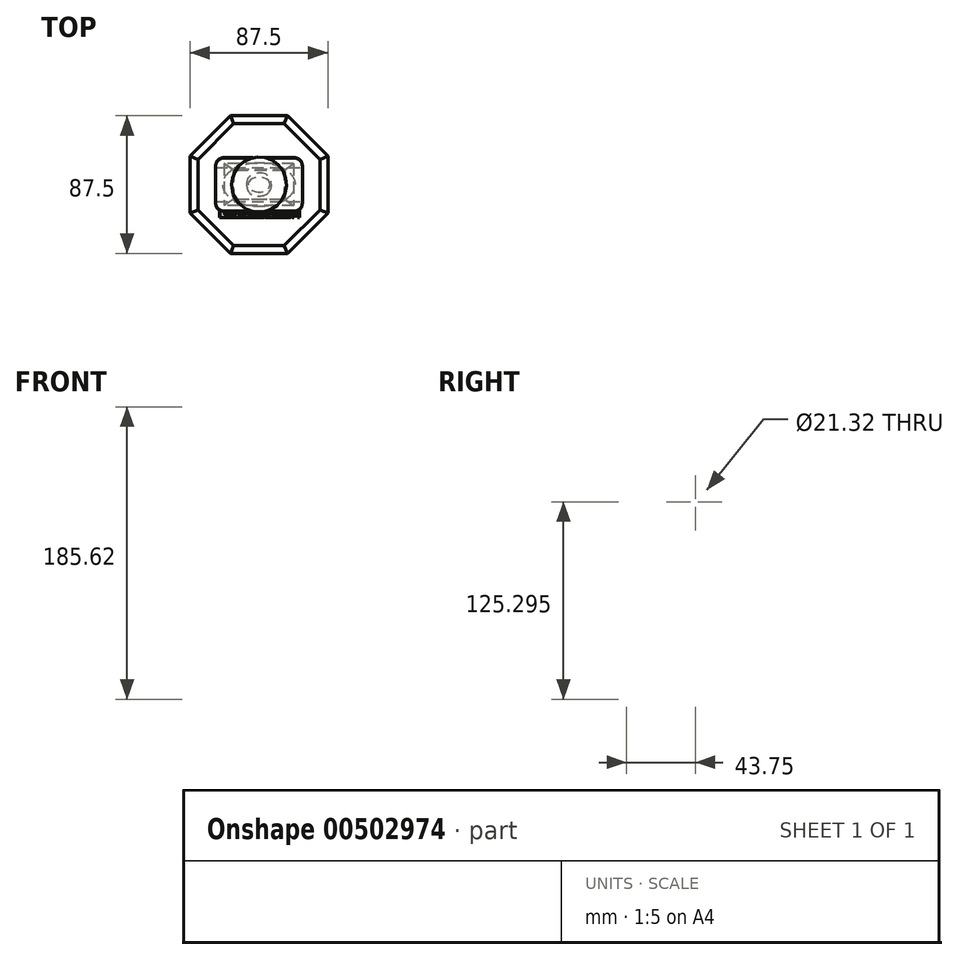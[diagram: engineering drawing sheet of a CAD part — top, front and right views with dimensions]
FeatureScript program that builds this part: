
annotation { "Feature Type Name" : "Feature", "Feature Type Description" : "" }
export const myFeature = defineFeature(function(context is Context, id is Id, definition is map)
    precondition{}
    {
        {
            var Q0;
            Q0=qCreatedBy(makeId("Top.planeOp"),FACE);
            cPlane(context, id + "F0", {"entities" : qUnion([Q0]), "cplaneType" : CPlaneType.OFFSET, "offset" : 60 * mm, "oppositeDirection" : true, "width" : 150 * mm, "height" : 150 * mm});
        }
        {
            var Q0;
            Q0=qCreatedBy(id+"F0.planeOp",FACE);
            var sketch = newSketch(context, id + "F1", { "sketchPlane" : qUnion([Q0])});
            skLineSegment(sketch, "E0.bottom", {"start": v(22.05, 13.3) * mm, "end": v(-22.05, 13.3) * mm});
            skLineSegment(sketch, "E0.top", {"start": v(22.05, -13.3) * mm, "end": v(-22.05, -13.3) * mm});
            skLineSegment(sketch, "E0.left", {"start": v(22.05, 13.3) * mm, "end": v(22.05, -13.3) * mm});
            skLineSegment(sketch, "E0.right", {"start": v(-22.05, 13.3) * mm, "end": v(-22.05, -13.3) * mm});
            skPoint(sketch, "E0.middle", {"position": v(0, 0) * mm});
            skSolve(sketch);
        }
        {
            var Q0;
            Q0=qCreatedBy(id+"F0.planeOp",FACE);
            cPlane(context, id + "F2", {"entities" : qUnion([Q0]), "cplaneType" : CPlaneType.OFFSET, "offset" : 30 * mm, "oppositeDirection" : true, "width" : 150 * mm, "height" : 150 * mm});
        }
        {
            var Q0;
            Q0=qCreatedBy(id+"F2.planeOp",FACE);
            var sketch = newSketch(context, id + "F3", { "sketchPlane" : qUnion([Q0])});
            skLineSegment(sketch, "E1.bottom", {"start": v(13.98, 7.39) * mm, "end": v(-13.98, 7.39) * mm});
            skLineSegment(sketch, "E1.top", {"start": v(13.98, -7.39) * mm, "end": v(-13.98, -7.39) * mm});
            skLineSegment(sketch, "E1.left", {"start": v(13.98, 7.39) * mm, "end": v(13.98, -7.39) * mm});
            skLineSegment(sketch, "E1.right", {"start": v(-13.98, 7.39) * mm, "end": v(-13.98, -7.39) * mm});
            skPoint(sketch, "E1.middle", {"position": v(0, 0) * mm});
            skSolve(sketch);
        }
        {
            var Q0;
            Q0=qCreatedBy(id+"F0.planeOp",FACE);
            cPlane(context, id + "F4", {"entities" : qUnion([Q0]), "cplaneType" : CPlaneType.OFFSET, "offset" : 10 * mm, "oppositeDirection" : true, "width" : 150 * mm, "height" : 150 * mm});
        }
        {
            var Q0;
            Q0=qCreatedBy(id+"F4.planeOp",FACE);
            var sketch = newSketch(context, id + "F5", { "sketchPlane" : qUnion([Q0])});
            skLineSegment(sketch, "E2.bottom", {"start": v(17.61, 10.11) * mm, "end": v(-17.61, 10.11) * mm});
            skLineSegment(sketch, "E2.top", {"start": v(17.61, -10.11) * mm, "end": v(-17.61, -10.11) * mm});
            skLineSegment(sketch, "E2.left", {"start": v(17.61, 10.11) * mm, "end": v(17.61, -10.11) * mm});
            skLineSegment(sketch, "E2.right", {"start": v(-17.61, 10.11) * mm, "end": v(-17.61, -10.11) * mm});
            skPoint(sketch, "E2.middle", {"position": v(0, 0) * mm});
            skSolve(sketch);
        }
        {
            var Q0;
            Q0=makeQuery(id+"F3.imprint","IMPRINT",FACE,{"disambiguationData":[TD([[makeQuery(id+"F3.imprint","IMPRINT",EDGE,{"derivedFrom":sQuery(id+"F3.wireOp",EDGE,"E1.bottom")}),1.0]])]});
            var Q1;
            Q1=makeQuery(id+"F5.imprint","IMPRINT",FACE,{"disambiguationData":[TD([[makeQuery(id+"F5.imprint","IMPRINT",EDGE,{"derivedFrom":sQuery(id+"F5.wireOp",EDGE,"E2.bottom")}),1.0]])]});
            var Q2;
            Q2=makeQuery(id+"F1.imprint","IMPRINT",FACE,{"disambiguationData":[TD([[makeQuery(id+"F1.imprint","IMPRINT",EDGE,{"derivedFrom":sQuery(id+"F1.wireOp",EDGE,"E0.bottom")}),1.0]])]});
            loft(context, id + "F6", {"sheetProfilesArray" : [{ "sheetProfileEntities" : qUnion([Q0]) }, { "sheetProfileEntities" : qUnion([Q1]) }, { "sheetProfileEntities" : qUnion([Q2]) }]});
        }
        {
            var Q0;
            Q0=qCreatedBy(id+"F0.planeOp",FACE);
            cPlane(context, id + "F7", {"entities" : qUnion([Q0]), "cplaneType" : CPlaneType.OFFSET, "offset" : 5 * mm, "width" : 150 * mm, "height" : 150 * mm});
        }
        {
            var Q0;
            Q0=qCreatedBy(id+"F7.planeOp",FACE);
            var sketch = newSketch(context, id + "F8", { "sketchPlane" : qUnion([Q0])});
            skLineSegment(sketch, "E3.bottom", {"start": v(16.62, 9.58) * mm, "end": v(-16.62, 9.58) * mm});
            skLineSegment(sketch, "E3.top", {"start": v(16.62, -9.58) * mm, "end": v(-16.62, -9.58) * mm});
            skLineSegment(sketch, "E3.left", {"start": v(16.62, 9.58) * mm, "end": v(16.62, -9.58) * mm});
            skLineSegment(sketch, "E3.right", {"start": v(-16.62, 9.58) * mm, "end": v(-16.62, -9.58) * mm});
            skPoint(sketch, "E3.middle", {"position": v(0, 0) * mm});
            skSolve(sketch);
        }
        {
            var Q1;
            Q1=makeQuery(id+"F8.imprint","IMPRINT",FACE,{"disambiguationData":[TD([[makeQuery(id+"F8.imprint","IMPRINT",EDGE,{"derivedFrom":sQuery(id+"F8.wireOp",EDGE,"E3.bottom")}),1.0]])]});
            var Q2;
            Q2=makeQuery(id+"F6.opLoft","CAP_FACE",FACE,{"disambiguationData":[OSD([makeQuery(id+"F1.imprint","IMPRINT",FACE,{"disambiguationData":[TD([[makeQuery(id+"F1.imprint","IMPRINT",EDGE,{"derivedFrom":sQuery(id+"F1.wireOp",EDGE,"E0.bottom")}),1.0]])]})])],"isStart":true});
            loft(context, id + "F9", {"operationType" : NewBodyOperationType.ADD, "sheetProfilesArray" : [{ "sheetProfileEntities" : qUnion([Q1]) }, { "sheetProfileEntities" : qUnion([Q2]) }]});
        }
        {
            var Q0;
            Q0=makeQuery(id+"F9.opLoft","CAP_FACE",FACE,{"disambiguationData":[OSD([makeQuery(id+"F8.imprint","IMPRINT",FACE,{"disambiguationData":[TD([[makeQuery(id+"F8.imprint","IMPRINT",EDGE,{"derivedFrom":sQuery(id+"F8.wireOp",EDGE,"E3.bottom")}),1.0]])]})])],"isStart":true});
            var sketch = newSketch(context, id + "F10", { "sketchPlane" : qUnion([Q0])});
            skSolve(sketch);
        }
        {
            var Q0;
            {var subQ0=sQuery(id+"F8.wireOp",EDGE,"E3.right");var subQ1=sQuery(id+"F8.wireOp",EDGE,"E3.left");var subQ2=sQuery(id+"F8.wireOp",EDGE,"E3.bottom");Q0=makeQuery(id+"F10.imprint","IMPRINT",FACE,{"disambiguationData":[TD([[makeQuery(id+"F10.imprint","IMPRINT",EDGE,{"derivedFrom":makeQuery(id+"F9.opLoft","MID_CAP_EDGE",EDGE,{"disambiguationData":[OSD([subQ2,subQ1,subQ0])],"capPos":0.0})}),-1.0]])]});}
            var sketch = newSketch(context, id + "F11", { "sketchPlane" : qUnion([Q0])});
            skEllipse(sketch, "E4", {"center": v(0, 0) * mm, "majorRadius": 6.96 * mm, "minorRadius": 4.81 * mm, "majorAxis": v(1, 0)});
            skSolve(sketch);
        }
        {
            var Q0;
            Q0=qCreatedBy(makeId("Top.planeOp"),FACE);
            var sketch = newSketch(context, id + "F12", { "sketchPlane" : qUnion([Q0])});
            skEllipse(sketch, "E5", {"center": v(0, 0) * mm, "majorRadius": 23.18 * mm, "minorRadius": 13.67 * mm, "majorAxis": v(1, 0)});
            skSolve(sketch);
        }
        {
            var Q0;
            Q0=qCreatedBy(makeId("Top.planeOp"),FACE);
            cPlane(context, id + "F13", {"entities" : qUnion([Q0]), "cplaneType" : CPlaneType.OFFSET, "offset" : 15 * mm, "oppositeDirection" : true, "width" : 150 * mm, "height" : 150 * mm});
        }
        {
            var Q0;
            Q0=qCreatedBy(id+"F13.planeOp",FACE);
            var sketch = newSketch(context, id + "F14", { "sketchPlane" : qUnion([Q0])});
            skEllipse(sketch, "E6", {"center": v(0, 0) * mm, "majorRadius": 15.9 * mm, "minorRadius": 9.58 * mm, "majorAxis": v(1, 0)});
            skSolve(sketch);
        }
        {
            var Q1;
            Q1=makeQuery(id+"F11.imprint","IMPRINT",FACE,{"disambiguationData":[TD([[makeQuery(id+"F11.imprint","IMPRINT",EDGE,{"derivedFrom":sQuery(id+"F11.wireOp",EDGE,"E4")}),1.0]])]});
            var Q2;
            Q2=makeQuery(id+"F14.imprint","IMPRINT",FACE,{"disambiguationData":[TD([[makeQuery(id+"F14.imprint","IMPRINT",EDGE,{"derivedFrom":sQuery(id+"F14.wireOp",EDGE,"E6")}),1.0]])]});
            var Q3;
            Q3=makeQuery(id+"F12.imprint","IMPRINT",FACE,{"disambiguationData":[TD([[makeQuery(id+"F12.imprint","IMPRINT",EDGE,{"derivedFrom":sQuery(id+"F12.wireOp",EDGE,"E5")}),1.0]])]});
            loft(context, id + "F15", {"operationType" : NewBodyOperationType.ADD, "sheetProfilesArray" : [{ "sheetProfileEntities" : qUnion([Q1]) }, { "sheetProfileEntities" : qUnion([Q2]) }, { "sheetProfileEntities" : qUnion([Q3]) }]});
        }
        {
            var Q0;
            Q0=qCreatedBy(makeId("Top.planeOp"),FACE);
            cPlane(context, id + "F16", {"entities" : qUnion([Q0]), "cplaneType" : CPlaneType.OFFSET, "offset" : 5 * mm, "width" : 150 * mm, "height" : 150 * mm});
        }
        {
            var Q0;
            Q0=qCreatedBy(makeId("Top.planeOp"),FACE);
            cPlane(context, id + "F17", {"entities" : qUnion([Q0]), "cplaneType" : CPlaneType.OFFSET, "offset" : 50 * mm, "width" : 150 * mm, "height" : 150 * mm});
        }
        {
            var Q0;
            Q0=qCreatedBy(id+"F17.planeOp",FACE);
            cPlane(context, id + "F18", {"entities" : qUnion([Q0]), "cplaneType" : CPlaneType.OFFSET, "offset" : 10 * mm, "width" : 150 * mm, "height" : 150 * mm});
        }
        {
            var Q0;
            Q0=qCreatedBy(id+"F16.planeOp",FACE);
            var sketch = newSketch(context, id + "F19", { "sketchPlane" : qUnion([Q0])});
            skLineSegment(sketch, "E7.bottom", {"start": v(22.5, -17.08) * mm, "end": v(-22.5, -17.08) * mm});
            skLineSegment(sketch, "E7.top", {"start": v(22.5, 17.08) * mm, "end": v(-22.5, 17.08) * mm});
            skLineSegment(sketch, "E7.left", {"start": v(27.5, -12.08) * mm, "end": v(27.5, 12.08) * mm});
            skLineSegment(sketch, "E7.right", {"start": v(-27.5, -12.08) * mm, "end": v(-27.5, 12.08) * mm});
            skPoint(sketch, "E7.middle", {"position": v(0, 0) * mm});
            skPoint(sketch, "E8.visualSharp", {"position": v(27.5, -17.08) * mm});
            skArc(sketch, "E8.filletArc", {"start": v(22.5, -17.08) * mm, "mid": v(26.04, -15.62) * mm, "end": v(27.5, -12.08) * mm});
            skPoint(sketch, "E9.visualSharp", {"position": v(27.5, 17.08) * mm});
            skArc(sketch, "E9.filletArc", {"start": v(27.5, 12.08) * mm, "mid": v(26.04, 15.62) * mm, "end": v(22.5, 17.08) * mm});
            skPoint(sketch, "E10.visualSharp", {"position": v(-27.5, 17.08) * mm});
            skArc(sketch, "E10.filletArc", {"start": v(-22.5, 17.08) * mm, "mid": v(-26.04, 15.62) * mm, "end": v(-27.5, 12.08) * mm});
            skPoint(sketch, "E11.visualSharp", {"position": v(-27.5, -17.08) * mm});
            skArc(sketch, "E11.filletArc", {"start": v(-27.5, -12.08) * mm, "mid": v(-26.04, -15.62) * mm, "end": v(-22.5, -17.08) * mm});
            skSolve(sketch);
        }
        {
            var Q0;
            Q0=qCreatedBy(id+"F17.planeOp",FACE);
            var sketch = newSketch(context, id + "F20", { "sketchPlane" : qUnion([Q0])});
            skLineSegment(sketch, "E12.bottom", {"start": v(22.5, -16.86) * mm, "end": v(-22.5, -16.86) * mm});
            skLineSegment(sketch, "E12.top", {"start": v(22.5, 16.86) * mm, "end": v(-22.5, 16.86) * mm});
            skLineSegment(sketch, "E12.left", {"start": v(27.5, -11.86) * mm, "end": v(27.5, 11.86) * mm});
            skLineSegment(sketch, "E12.right", {"start": v(-27.5, -11.86) * mm, "end": v(-27.5, 11.86) * mm});
            skPoint(sketch, "E12.middle", {"position": v(0, 0) * mm});
            skPoint(sketch, "E13.visualSharp", {"position": v(27.5, 16.86) * mm});
            skArc(sketch, "E13.filletArc", {"start": v(27.5, 11.86) * mm, "mid": v(26.04, 15.4) * mm, "end": v(22.5, 16.86) * mm});
            skPoint(sketch, "E14.visualSharp", {"position": v(27.5, -16.86) * mm});
            skArc(sketch, "E14.filletArc", {"start": v(22.5, -16.86) * mm, "mid": v(26.04, -15.4) * mm, "end": v(27.5, -11.86) * mm});
            skPoint(sketch, "E15.visualSharp", {"position": v(-27.5, -16.86) * mm});
            skArc(sketch, "E15.filletArc", {"start": v(-27.5, -11.86) * mm, "mid": v(-26.04, -15.4) * mm, "end": v(-22.5, -16.86) * mm});
            skPoint(sketch, "E16.visualSharp", {"position": v(-27.5, 16.86) * mm});
            skArc(sketch, "E16.filletArc", {"start": v(-22.5, 16.86) * mm, "mid": v(-26.04, 15.4) * mm, "end": v(-27.5, 11.86) * mm});
            skSolve(sketch);
        }
        {
            var Q0;
            Q0=qCreatedBy(id+"F18.planeOp",FACE);
            var sketch = newSketch(context, id + "F21", { "sketchPlane" : qUnion([Q0])});
            skEllipse(sketch, "E17", {"center": v(0, 0) * mm, "majorRadius": 6.6 * mm, "minorRadius": 6.54 * mm, "majorAxis": v(1, 0)});
            skSolve(sketch);
        }
        {
            var Q1;
            Q1=makeQuery(id+"F15.opLoft","CAP_FACE",FACE,{"disambiguationData":[OSD([makeQuery(id+"F12.imprint","IMPRINT",FACE,{"disambiguationData":[TD([[makeQuery(id+"F12.imprint","IMPRINT",EDGE,{"derivedFrom":sQuery(id+"F12.wireOp",EDGE,"E5")}),1.0]])]})])],"isStart":true});
            var Q2;
            Q2=makeQuery(id+"F19.imprint","IMPRINT",FACE,{"disambiguationData":[TD([[makeQuery(id+"F19.imprint","IMPRINT",EDGE,{"derivedFrom":sQuery(id+"F19.wireOp",EDGE,"E7.bottom")}),-1.0]])]});
            loft(context, id + "F22", {"operationType" : NewBodyOperationType.ADD, "sheetProfilesArray" : [{ "sheetProfileEntities" : qUnion([Q1]) }, { "sheetProfileEntities" : qUnion([Q2]) }]});
        }
        {
            var Q1;
            Q1=makeQuery(id+"F22.opLoft","CAP_FACE",FACE,{"disambiguationData":[OSD([makeQuery(id+"F19.imprint","IMPRINT",FACE,{"disambiguationData":[TD([[makeQuery(id+"F19.imprint","IMPRINT",EDGE,{"derivedFrom":sQuery(id+"F19.wireOp",EDGE,"E7.bottom")}),-1.0]])]})])],"isStart":true});
            var Q2;
            Q2=makeQuery(id+"F20.imprint","IMPRINT",FACE,{"disambiguationData":[TD([[makeQuery(id+"F20.imprint","IMPRINT",EDGE,{"derivedFrom":sQuery(id+"F20.wireOp",EDGE,"E12.bottom")}),-1.0]])]});
            loft(context, id + "F23", {"operationType" : NewBodyOperationType.ADD, "sheetProfilesArray" : [{ "sheetProfileEntities" : qUnion([Q1]) }, { "sheetProfileEntities" : qUnion([Q2]) }]});
        }
        {
            var Q1;
            Q1=makeQuery(id+"F23.opLoft","CAP_FACE",FACE,{"disambiguationData":[OSD([makeQuery(id+"F20.imprint","IMPRINT",FACE,{"disambiguationData":[TD([[makeQuery(id+"F20.imprint","IMPRINT",EDGE,{"derivedFrom":sQuery(id+"F20.wireOp",EDGE,"E12.bottom")}),-1.0]])]})])],"isStart":true});
            var Q2;
            Q2=makeQuery(id+"F21.imprint","IMPRINT",FACE,{"disambiguationData":[TD([[makeQuery(id+"F21.imprint","IMPRINT",EDGE,{"derivedFrom":sQuery(id+"F21.wireOp",EDGE,"E17")}),1.0]])]});
            loft(context, id + "F24", {"operationType" : NewBodyOperationType.ADD, "sheetProfilesArray" : [{ "sheetProfileEntities" : qUnion([Q1]) }, { "sheetProfileEntities" : qUnion([Q2]) }]});
        }
        {
            var Q0;
            Q0=qCreatedBy(makeId("Front.planeOp"),FACE);
            var sketch = newSketch(context, id + "F25", { "sketchPlane" : qUnion([Q0])});
            skArc(sketch, "E18", {"start": v(0, 95.62) * mm, "mid": v(-17.5, 76.12) * mm, "end": v(0, 56.62) * mm});
            skLineSegment(sketch, "E19", {"start": v(0, 95.62) * mm, "end": v(0, 56.62) * mm});
            skSolve(sketch);
        }
        {
            var Q0;
            Q0 = qSketchRegion(id + "F25", true);
            var Q1;
            Q1=sQuery(id+"F25.wireOp",EDGE,"E19");
            revolve(context, id + "F26", {"operationType" : NewBodyOperationType.ADD, "entities" : qUnion([Q0]), "axis" : qUnion([Q1]), "revolveType" : RevolveType.FULL});
        }
        {
            var Q0;
            Q0=makeQuery(id+"F23.opLoft","SWEPT_FACE",FACE,{"disambiguationData":[OSD([sQuery(id+"F19.wireOp",EDGE,"E7.left"),sQuery(id+"F19.wireOp",EDGE,"E8.filletArc"),sQuery(id+"F19.wireOp",EDGE,"E9.filletArc"),sQuery(id+"F20.wireOp",EDGE,"E12.left"),sQuery(id+"F20.wireOp",EDGE,"E13.filletArc"),sQuery(id+"F20.wireOp",EDGE,"E14.filletArc")])]});
            var sketch = newSketch(context, id + "F27", { "sketchPlane" : qUnion([Q0])});
            skCircle(sketch, "E20", {"center": v(0, 35.3) * mm, "radius": 10.66 * mm});
            skSolve(sketch);
        }
        {
            var Q0;
            Q0=makeQuery(id+"F27.imprint","IMPRINT",FACE,{"disambiguationData":[TD([[makeQuery(id+"F27.imprint","IMPRINT",EDGE,{"derivedFrom":sQuery(id+"F27.wireOp",EDGE,"E20")}),1.0]])]});
            var Q1;
            Q1=sQuery(id+"F27.wireOp",EDGE,"E20");
            extrude(context, id + "F28", {"entities" : qUnion([Q0]), "operationType" : NewBodyOperationType.REMOVE, "surfaceEntities" : qUnion([Q1]), "oppositeDirection" : true, "depth" : 60 * mm});
        }
        {
            var Q0;
            Q0=makeQuery(id+"F23.opLoft","SWEPT_FACE",FACE,{"disambiguationData":[OSD([sQuery(id+"F19.wireOp",EDGE,"E7.bottom"),sQuery(id+"F19.wireOp",EDGE,"E8.filletArc"),sQuery(id+"F19.wireOp",EDGE,"E11.filletArc"),sQuery(id+"F20.wireOp",EDGE,"E12.bottom"),sQuery(id+"F20.wireOp",EDGE,"E14.filletArc"),sQuery(id+"F20.wireOp",EDGE,"E15.filletArc")])]});
            var sketch = newSketch(context, id + "F29", { "sketchPlane" : qUnion([Q0])});
            skText(sketch, "E21", { "text": "Foosball", "fontName": "OpenSans-Regular.ttf"});
            const initialGuessF29  = {"E21": [-0.02642, 0.02326, 1, 0, 0.0099]};
            skSetInitialGuess(sketch, initialGuessF29);
            skSolve(sketch);
        }
        {
            var Q0;
            Q0 = qSketchRegion(id + "F29", true);
            var Q1;
            Q1=makeQuery(id+"F6.opLoft","SWEPT_BODY",BODY,{"disambiguationData":[OSD([makeQuery(id+"F1.imprint","IMPRINT",FACE,{"disambiguationData":[TD([[makeQuery(id+"F1.imprint","IMPRINT",EDGE,{"derivedFrom":sQuery(id+"F1.wireOp",EDGE,"E0.bottom")}),1.0]])]}),makeQuery(id+"F3.imprint","IMPRINT",FACE,{"disambiguationData":[TD([[makeQuery(id+"F3.imprint","IMPRINT",EDGE,{"derivedFrom":sQuery(id+"F3.wireOp",EDGE,"E1.bottom")}),1.0]])]}),sQuery(id+"F5.wireOp",EDGE,"E2.bottom")])]});
            extrude(context, id + "F30", {"entities" : qUnion([Q0]), "operationType" : NewBodyOperationType.ADD, "oppositeDirection" : true, "endBoundEntityBody" : qUnion([Q1]), "depth" : 3 * mm});
        }
        {
            var Q0;
            Q0 = qSketchRegion(id + "F29", true);
            extrude(context, id + "F31", {"entities" : qUnion([Q0]), "operationType" : NewBodyOperationType.ADD, "depth" : 4 * mm});
        }
        {
            var Q0;
            {var subQ0=sQuery(id+"F29.wireOp",EDGE,"E21.sketch_text.stroke-8");var subQ1=sQuery(id+"F29.wireOp",EDGE,"E21.sketch_text.stroke-4");var subQ2=sQuery(id+"F29.wireOp",EDGE,"E21.sketch_text.stroke-2");var subQ3=sQuery(id+"F29.wireOp",EDGE,"E21.sketch_text.stroke-7");var subQ4=sQuery(id+"F29.wireOp",EDGE,"E21.sketch_text.stroke-6");var subQ5=sQuery(id+"F29.wireOp",EDGE,"E21.sketch_text.stroke-3");var subQ6=sQuery(id+"F20.wireOp",EDGE,"E14.filletArc");var subQ8=sQuery(id+"F20.wireOp",EDGE,"E12.bottom");var subQ9=sQuery(id+"F19.wireOp",EDGE,"E8.filletArc");var subQ11=sQuery(id+"F19.wireOp",EDGE,"E7.bottom");var subQ12=sQuery(id+"F20.wireOp",EDGE,"E15.filletArc");var subQ13=sQuery(id+"F19.wireOp",EDGE,"E11.filletArc");Q0=makeQuery(id+"F31.boolean.opBoolean","SPLIT",FACE,{"disambiguationData":[TD([makeQuery(id+"F30.opExtrude","SWEPT_FACE",FACE,{"disambiguationData":[OSD([subQ2])]})])],"derivedFrom":makeQuery(id+"F30.boolean.opBoolean","MERGE",FACE,{"derivedFrom":[makeQuery(id+"F23.opLoft","SWEPT_FACE",FACE,{"disambiguationData":[OSD([subQ11,subQ9,subQ13,subQ8,subQ6,subQ12])]}),makeQuery(id+"F30.opExtrude","CAP_FACE",FACE,{"disambiguationData":[OSD([sQuery(id+"F29.wireOp",EDGE,"E21.sketch_text.stroke-0"),sQuery(id+"F29.wireOp",EDGE,"E21.sketch_text.stroke-1"),subQ2,subQ5,subQ1,sQuery(id+"F29.wireOp",EDGE,"E21.sketch_text.stroke-5"),subQ4,subQ3,subQ0,sQuery(id+"F29.wireOp",EDGE,"E21.sketch_text.stroke-9")])],"isStart":true})]})});}
            var sketch = newSketch(context, id + "F32", { "sketchPlane" : qUnion([Q0])});
            skText(sketch, "E22", { "text": "OneView", "fontName": "OpenSans-Regular.ttf"});
            const initialGuessF32  = {"E22": [-0.02263, 0.03828, 1, 0, 0.00778]};
            skSetInitialGuess(sketch, initialGuessF32);
            skSolve(sketch);
        }
        {
            var Q0;
            Q0 = qSketchRegion(id + "F32", true);
            extrude(context, id + "F33", {"entities" : qUnion([Q0]), "operationType" : NewBodyOperationType.ADD, "depth" : 2 * mm});
        }
        {
            var Q0;
            {var subQ21=sQuery(id+"F20.wireOp",EDGE,"E14.filletArc");var subQ23=sQuery(id+"F20.wireOp",EDGE,"E12.bottom");var subQ37=sQuery(id+"F19.wireOp",EDGE,"E8.filletArc");var subQ39=sQuery(id+"F19.wireOp",EDGE,"E7.bottom");var subQ49=sQuery(id+"F29.wireOp",EDGE,"E21.sketch_text.stroke-8");var subQ52=sQuery(id+"F20.wireOp",EDGE,"E15.filletArc");var subQ53=sQuery(id+"F19.wireOp",EDGE,"E11.filletArc");var subQ56=sQuery(id+"F29.wireOp",EDGE,"E21.sketch_text.stroke-6");var subQ59=sQuery(id+"F29.wireOp",EDGE,"E21.sketch_text.stroke-4");var subQ68=sQuery(id+"F29.wireOp",EDGE,"E21.sketch_text.stroke-2");var subQ76=sQuery(id+"F29.wireOp",EDGE,"E21.sketch_text.stroke-3");var subQ81=sQuery(id+"F29.wireOp",EDGE,"E21.sketch_text.stroke-7");var subQ84=makeQuery(id+"F30.opExtrude","SWEPT_FACE",FACE,{"disambiguationData":[OSD([subQ68])]});Q0=makeQuery(id+"F33.boolean.opBoolean","SPLIT",FACE,{"disambiguationData":[TD([subQ84])],"derivedFrom":makeQuery(id+"F31.boolean.opBoolean","SPLIT",FACE,{"disambiguationData":[TD([subQ84])],"derivedFrom":makeQuery(id+"F30.boolean.opBoolean","MERGE",FACE,{"derivedFrom":[makeQuery(id+"F23.opLoft","SWEPT_FACE",FACE,{"disambiguationData":[OSD([subQ39,subQ37,subQ53,subQ23,subQ21,subQ52])]}),makeQuery(id+"F30.opExtrude","CAP_FACE",FACE,{"disambiguationData":[OSD([sQuery(id+"F29.wireOp",EDGE,"E21.sketch_text.stroke-0"),sQuery(id+"F29.wireOp",EDGE,"E21.sketch_text.stroke-1"),subQ68,subQ76,subQ59,sQuery(id+"F29.wireOp",EDGE,"E21.sketch_text.stroke-5"),subQ56,subQ81,subQ49,sQuery(id+"F29.wireOp",EDGE,"E21.sketch_text.stroke-9")])],"isStart":true})]})})});}
            var sketch = newSketch(context, id + "F34", { "sketchPlane" : qUnion([Q0])});
            skText(sketch, "E23", { "text": "Champion", "fontName": "OpenSans-Bold.ttf"});
            const initialGuessF34  = {"E23": [-0.0195, 0.01177, 1, 0, 0.00566]};
            skSetInitialGuess(sketch, initialGuessF34);
            skSolve(sketch);
        }
        {
            var Q0;
            Q0 = qSketchRegion(id + "F34", true);
            extrude(context, id + "F35", {"entities" : qUnion([Q0]), "operationType" : NewBodyOperationType.ADD, "depth" : 4 * mm});
        }
        {
            var Q0;
            Q0=makeQuery(id+"F6.opLoft","CAP_FACE",FACE,{"disambiguationData":[OSD([makeQuery(id+"F3.imprint","IMPRINT",FACE,{"disambiguationData":[TD([[makeQuery(id+"F3.imprint","IMPRINT",EDGE,{"derivedFrom":sQuery(id+"F3.wireOp",EDGE,"E1.bottom")}),1.0]])]})])],"isStart":true});
            var sketch = newSketch(context, id + "F36", { "sketchPlane" : qUnion([Q0])});
            skCircle(sketch, "E24.cCircle", {"center": v(0, 0) * mm, "radius": 43.75 * mm, "construction": true});
            skLineSegment(sketch, "E24.0", {"start": v(18.12, -43.75) * mm, "end": v(-18.12, -43.75) * mm});
            skLineSegment(sketch, "E24.1", {"start": v(-18.12, -43.75) * mm, "end": v(-43.75, -18.12) * mm});
            skLineSegment(sketch, "E24.2", {"start": v(-43.75, -18.12) * mm, "end": v(-43.75, 18.12) * mm});
            skLineSegment(sketch, "E24.3", {"start": v(-43.75, 18.12) * mm, "end": v(-18.12, 43.75) * mm});
            skLineSegment(sketch, "E24.4", {"start": v(-18.12, 43.75) * mm, "end": v(18.12, 43.75) * mm});
            skLineSegment(sketch, "E24.5", {"start": v(18.12, 43.75) * mm, "end": v(43.75, 18.12) * mm});
            skLineSegment(sketch, "E24.6", {"start": v(43.75, 18.12) * mm, "end": v(43.75, -18.12) * mm});
            skLineSegment(sketch, "E24.7", {"start": v(43.75, -18.12) * mm, "end": v(18.12, -43.75) * mm});
            skPoint(sketch, "E24.0.midPoint", {"position": v(0, -43.75) * mm});
            skSolve(sketch);
        }
        {
            var Q0;
            Q0 = qSketchRegion(id + "F36", true);
            extrude(context, id + "F37", {"entities" : qUnion([Q0]), "operationType" : NewBodyOperationType.ADD, "oppositeDirection" : true, "depth" : 15 * mm});
        }
        {
            var Q0;
            Q0=makeQuery(id+"F37.opExtrude","CAP_EDGE",EDGE,{"disambiguationData":[OSD([sQuery(id+"F36.wireOp",EDGE,"E24.5")])],"isStart":false});
            var Q1;
            Q1=makeQuery(id+"F37.opExtrude","CAP_EDGE",EDGE,{"disambiguationData":[OSD([sQuery(id+"F36.wireOp",EDGE,"E24.4")])],"isStart":false});
            var Q2;
            Q2=makeQuery(id+"F37.opExtrude","CAP_EDGE",EDGE,{"disambiguationData":[OSD([sQuery(id+"F36.wireOp",EDGE,"E24.3")])],"isStart":false});
            var Q3;
            Q3=makeQuery(id+"F37.opExtrude","CAP_EDGE",EDGE,{"disambiguationData":[OSD([sQuery(id+"F36.wireOp",EDGE,"E24.2")])],"isStart":false});
            var Q4;
            Q4=makeQuery(id+"F37.opExtrude","CAP_EDGE",EDGE,{"disambiguationData":[OSD([sQuery(id+"F36.wireOp",EDGE,"E24.1")])],"isStart":false});
            var Q5;
            Q5=makeQuery(id+"F37.opExtrude","CAP_EDGE",EDGE,{"disambiguationData":[OSD([sQuery(id+"F36.wireOp",EDGE,"E24.7")])],"isStart":false});
            var Q6;
            Q6=makeQuery(id+"F37.opExtrude","CAP_EDGE",EDGE,{"disambiguationData":[OSD([sQuery(id+"F36.wireOp",EDGE,"E24.6")])],"isStart":false});
            var Q7;
            Q7=makeQuery(id+"F37.opExtrude","CAP_EDGE",EDGE,{"disambiguationData":[OSD([sQuery(id+"F36.wireOp",EDGE,"E24.0")])],"isStart":false});
            chamfer(context, id + "F38", {"entities" : qUnion([Q0, Q1, Q2, Q3, Q4, Q5, Q6, Q7]), "width" : 5 * mm, "tangentPropagation" : true});
        }
    });
